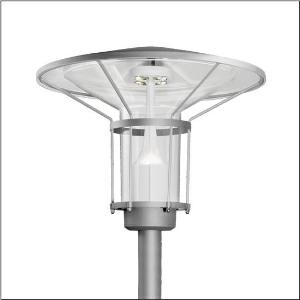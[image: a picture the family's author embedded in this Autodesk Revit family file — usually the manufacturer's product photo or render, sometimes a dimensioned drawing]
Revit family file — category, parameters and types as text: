
# Revit family: laterne_classic_iq___p1_0a_5xa5245ff14hp_7b29
name_source: partatom
category: Lighting Fixtures
units: mm (PartAtom-declared; Revit-internal decimal feet)

## family parameters
Cut with Voids When Loaded = No
Host = Face
Light Source = No
Part Type = Normal
Room Calculation Point = No
Round Connector Dimension = Use Diameter
Shared = No

## types (1)
- --- (1 x LED, 4210 lm, 33.6 W, 3000K)
    Apparent Load = 34 VA
    CIE Flux Codes = 31 61 91 96 100
    Color Rendering = 70
    Color Temperature = 3000K
    Default Elevation = 1800 mm
    Description = Lantern Classic iQ, mast luminaire, Module 540 iQ-SR, primary light control with 3 zone facetted reflector, of plastic, silver coated, highly specular, structured, primary optical cover: cover, of PMMA, transparent, light distribution: P1.0a, light emission: direct distribution, primary light characteristic: strongly asymmetric, installation type: post-top, LED, High Power LED, rated luminous flux: 4.210lm, luminous efficacy: 125lm/W, light colour: 730, colour temperature: 3000K, control gear: ECG iQ, control: presetting dimming logarithmic, Street-Remote, Auto-Match, Temp-Guard, Lumen-Switch, Night-Set, Smart-Wire, Light-Fading, Desk-Remote (wireless, voltage-free reading and setting of iQ features in the workshop via application-optimized NFC function/RFID function), optimised constant luminous flux control (CLO 2.0), with terminal, 6-pole, max. 2.5mm², mains connection: 230..240V, AC, 50/60Hz, start of lifetime: 34W, end of service life: 36W, reduction: 15W, luminaire housing, upper part, of glass-fibre reinforced polyester, coated, Siteco® metallic grey (DB 702S), diameter: 750mm, height: 596mm, spigot size: d x l = 76 x 70mm (post-top) | with reducer (optional accessory) 60 x 70mm, post-top mast mounting element, of diecast aluminium, coated, Siteco® metallic grey (DB 702S), Module 540 iQ-SR, traffic white (RAL 9016), equipment: Power, protection rating (complete): IP65, insulation class (complete): insulation class II (safety insulation), certification: CE, ENEC, VDE, packaging unit: 1 piece

Light Distribution: P1.0a
    Height = 596 mm
    Lamp = 1 x LED
    Lamp Light Flux = 4210 lm
    Lamp Power = 33.6 W
    Lamp count = 1
    Length = 750 mm
    Luminous efficacy = 125 lm/W
    Manufacturer = Siteco
    ModVariant = No
    Model = 5XA5245FF14HP
    Number of Poles = 1
    OnlyDefault = Yes
    Power Factor = 1
    Product Name = Laterne Classic iQ | P1.0a
    Product group = mast luminaire | pylon top
    ProductGroupID = 6100
    Protection Class = Protection class II
    Protection Degree = IP 65
    RLX_Detail_Level = 1
    RLX_Emergency_Light_Flux = 0 lm
    RLX_Emergency_Type = 0
    RLX_Emergency_Type_DB = No
    RlxData = <blob elided: 65645 chars, md5=23666f37>
    Socket = socket
    Standby Power = 0 W
    System Light Flux = 4210 lm
    System Power = 34 W
    Type Comments = factory setting: luminous flux: 100 % | dim-lin: 254 | 695 mA
    Type Image = l_1006052.jpg
    URL = http://relux.com
    VarID = @adj_145809
    Voltage = 0 V
    Weight = 0.00 kg
    Width = 0 mm  [stored 0 ft]

note: [stored X ft] marks values corroborated as IEEE doubles in the binary element streams (Revit-internal decimal feet)

## geometry (parser evidence)
native form markers: Blend x4, Sweep x11
no freeform markers — native parametric forms only
